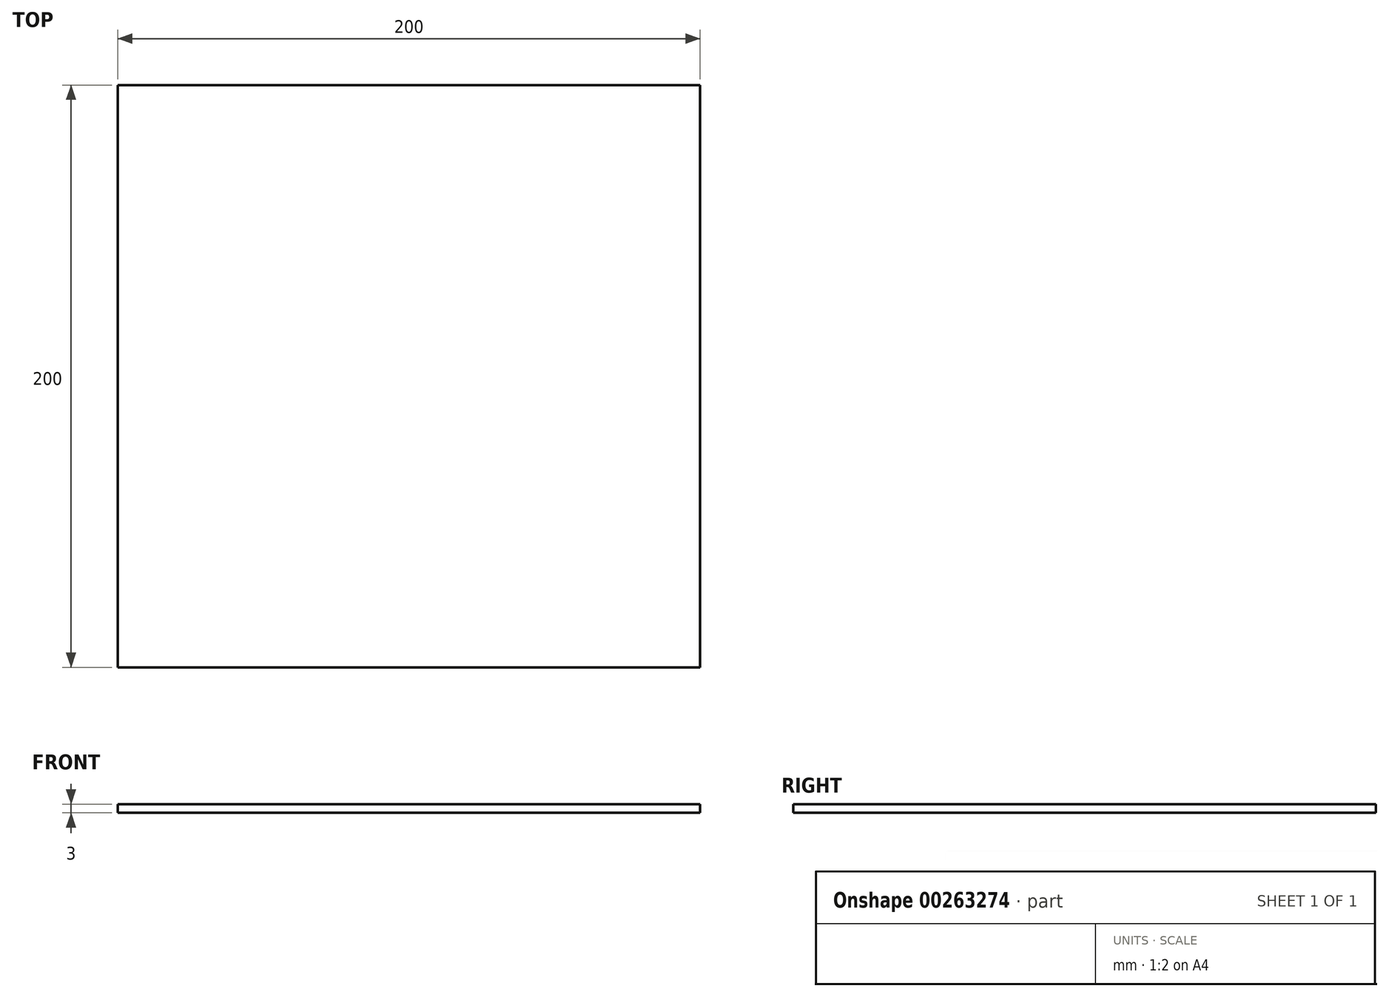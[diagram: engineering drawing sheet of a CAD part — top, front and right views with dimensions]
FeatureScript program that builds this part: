
annotation { "Feature Type Name" : "Feature", "Feature Type Description" : "" }
export const myFeature = defineFeature(function(context is Context, id is Id, definition is map)
    precondition{}
    {
        {
            var Q0;
            Q0=qCreatedBy(makeId("Top.planeOp"),FACE);
            var sketch = newSketch(context, id + "F0", { "sketchPlane" : qUnion([Q0])});
            skLineSegment(sketch, "E0.bottom", {"start": v(100, -100) * mm, "end": v(-100, -100) * mm});
            skLineSegment(sketch, "E0.top", {"start": v(100, 100) * mm, "end": v(-100, 100) * mm});
            skLineSegment(sketch, "E0.left", {"start": v(100, -100) * mm, "end": v(100, 100) * mm});
            skLineSegment(sketch, "E0.right", {"start": v(-100, -100) * mm, "end": v(-100, 100) * mm});
            skPoint(sketch, "E0.middle", {"position": v(0, 0) * mm});
            skSolve(sketch);
        }
        {
            var Q0;
            Q0 = qSketchRegion(id + "F0", true);
            extrude(context, id + "F1", {"entities" : qUnion([Q0]), "depth" : 3 * mm});
        }
    });
